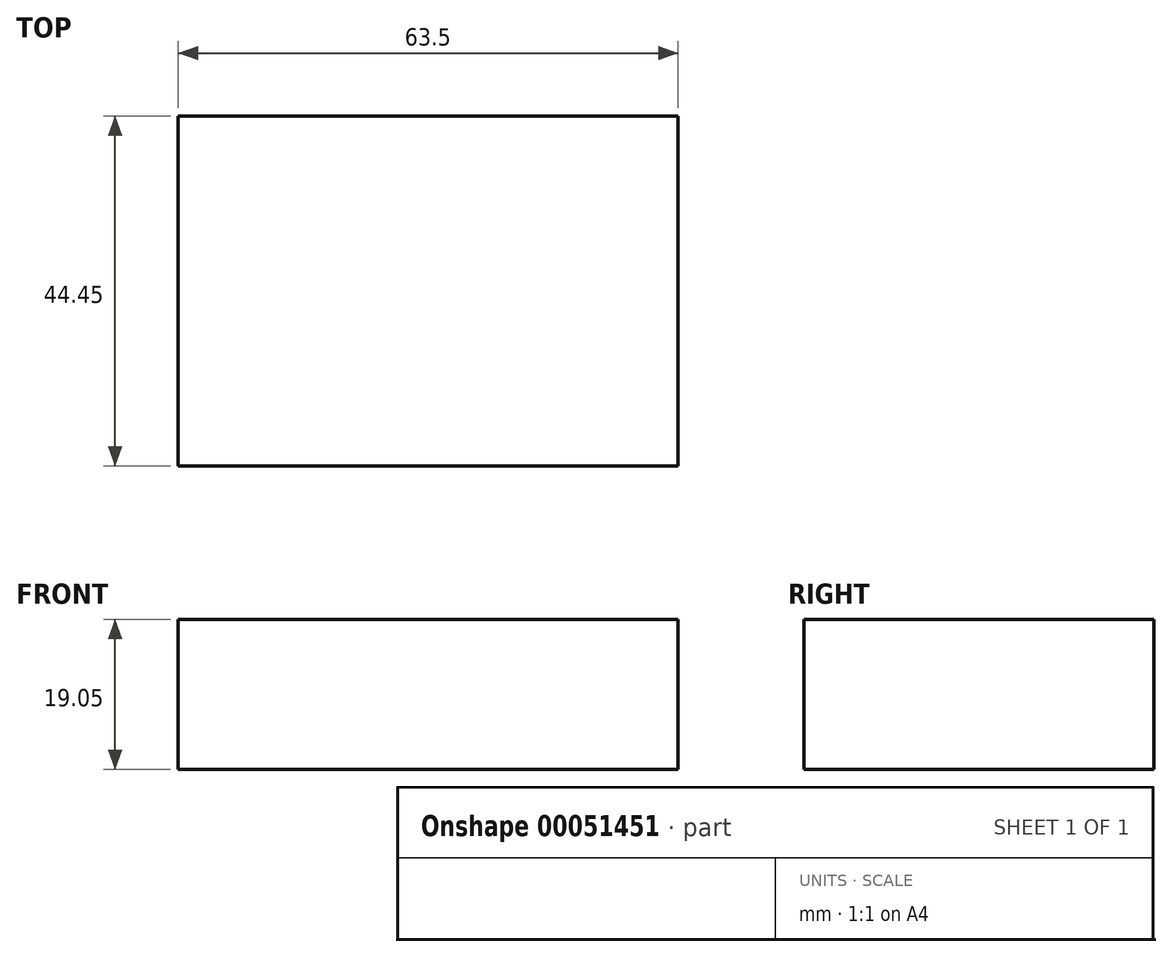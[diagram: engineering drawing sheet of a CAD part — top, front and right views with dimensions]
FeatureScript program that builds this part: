
annotation { "Feature Type Name" : "Feature", "Feature Type Description" : "" }
export const myFeature = defineFeature(function(context is Context, id is Id, definition is map)
    precondition{}
    {
        {
            var Q0;
            Q0=qCreatedBy(makeId("Front.planeOp"),FACE);
            var sketch = newSketch(context, id + "F0", { "sketchPlane" : qUnion([Q0])});
            skLineSegment(sketch, "E0.bottom", {"start": v(-30.2, 1.37) * mm, "end": v(33.3, 1.37) * mm});
            skLineSegment(sketch, "E0.top", {"start": v(-30.2, -17.68) * mm, "end": v(33.3, -17.68) * mm});
            skLineSegment(sketch, "E0.left", {"start": v(-30.2, 1.37) * mm, "end": v(-30.2, -17.68) * mm});
            skLineSegment(sketch, "E0.right", {"start": v(33.3, 1.37) * mm, "end": v(33.3, -17.68) * mm});
            skSolve(sketch);
        }
        {
            var Q0;
            Q0=makeQuery(id+"F0.imprint","IMPRINT",FACE,{"disambiguationData":[TD([[makeQuery(id+"F0.imprint","IMPRINT",EDGE,{"derivedFrom":sQuery(id+"F0.wireOp",EDGE,"E0.bottom")}),-1.0]])]});
            extrude(context, id + "F1", {"entities" : qUnion([Q0]), "depth" : 44.45 * mm});
        }
    });
